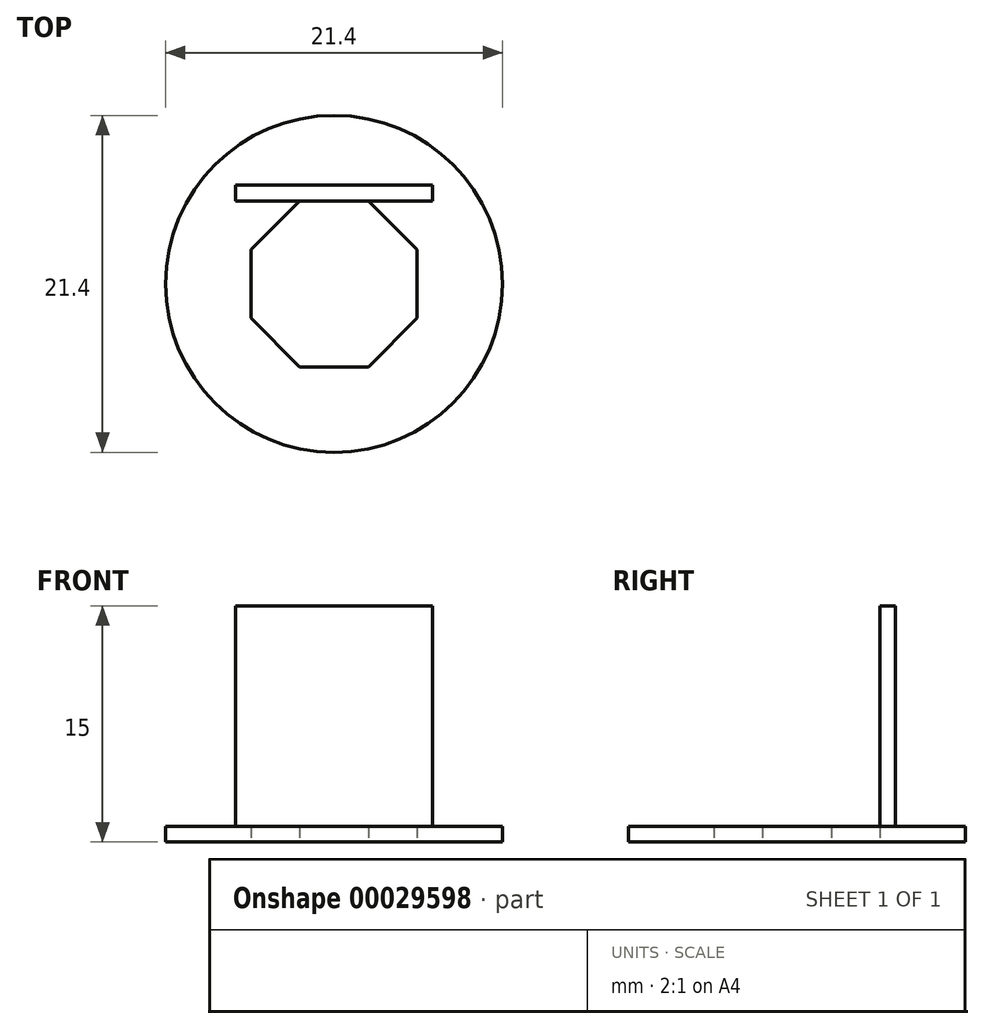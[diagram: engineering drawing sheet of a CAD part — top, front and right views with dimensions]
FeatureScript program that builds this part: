
annotation { "Feature Type Name" : "Feature", "Feature Type Description" : "" }
export const myFeature = defineFeature(function(context is Context, id is Id, definition is map)
    precondition{}
    {
        {
            var Q0;
            Q0=qCreatedBy(makeId("Top.planeOp"),FACE);
            var sketch = newSketch(context, id + "F0", { "sketchPlane" : qUnion([Q0])});
            skCircle(sketch, "E0", {"center": v(0, 0) * mm, "radius": 5.7 * mm});
            skCircle(sketch, "E1.0", {"center": v(0, 0) * mm, "radius": 10.7 * mm});
            skLineSegment(sketch, "E2", {"start": v(0, 5.7) * mm, "end": v(0, -5.7) * mm, "construction": true});
            skLineSegment(sketch, "E3", {"start": v(0, 0) * mm, "end": v(5.7, 0) * mm, "construction": true});
            skLineSegment(sketch, "E4", {"start": v(5.7, 0) * mm, "end": v(0, 5.7) * mm, "construction": true});
            skLineSegment(sketch, "E5", {"start": v(0, 0) * mm, "end": v(4.03, 4.03) * mm, "construction": true});
            skLineSegment(sketch, "E6", {"start": v(0, 5.7) * mm, "end": v(4.03, 4.03) * mm, "construction": true});
            skLineSegment(sketch, "E7", {"start": v(0, 0) * mm, "end": v(2.18, 5.27) * mm, "construction": true});
            skCircle(sketch, "E8.cCircle", {"center": v(0, 0) * mm, "radius": 5.7 * mm, "construction": true});
            skLineSegment(sketch, "E8.0", {"start": v(2.18, 5.27) * mm, "end": v(5.27, 2.18) * mm});
            skLineSegment(sketch, "E8.1", {"start": v(5.27, 2.18) * mm, "end": v(5.27, -2.18) * mm});
            skLineSegment(sketch, "E8.2", {"start": v(5.27, -2.18) * mm, "end": v(2.18, -5.27) * mm});
            skLineSegment(sketch, "E8.3", {"start": v(2.18, -5.27) * mm, "end": v(-2.18, -5.27) * mm});
            skLineSegment(sketch, "E8.4", {"start": v(-2.18, -5.27) * mm, "end": v(-5.27, -2.18) * mm});
            skLineSegment(sketch, "E8.5", {"start": v(-5.27, -2.18) * mm, "end": v(-5.27, 2.18) * mm});
            skLineSegment(sketch, "E8.6", {"start": v(-5.27, 2.18) * mm, "end": v(-2.18, 5.27) * mm});
            skLineSegment(sketch, "E8.7", {"start": v(-2.18, 5.27) * mm, "end": v(2.18, 5.27) * mm});
            skSolve(sketch);
        }
        {
            var Q0;
            {var subQ0=sQuery(id+"F0.wireOp",EDGE,"E8.6");Q0=makeQuery(id+"F0.imprint","IMPRINT",FACE,{"disambiguationData":[TD([[makeQuery(id+"F0.imprint","IMPRINT",EDGE,{"derivedFrom":subQ0}),1.0]])]});}
            var Q1;
            {var subQ0=sQuery(id+"F0.wireOp",EDGE,"E8.4");Q1=makeQuery(id+"F0.imprint","IMPRINT",FACE,{"disambiguationData":[TD([[makeQuery(id+"F0.imprint","IMPRINT",EDGE,{"derivedFrom":subQ0}),1.0]])]});}
            var Q2;
            {var subQ0=sQuery(id+"F0.wireOp",EDGE,"E8.3");Q2=makeQuery(id+"F0.imprint","IMPRINT",FACE,{"disambiguationData":[TD([[makeQuery(id+"F0.imprint","IMPRINT",EDGE,{"derivedFrom":subQ0}),1.0]])]});}
            var Q3;
            {var subQ0=sQuery(id+"F0.wireOp",EDGE,"E8.1");Q3=makeQuery(id+"F0.imprint","IMPRINT",FACE,{"disambiguationData":[TD([[makeQuery(id+"F0.imprint","IMPRINT",EDGE,{"derivedFrom":subQ0}),1.0]])]});}
            var Q4;
            Q4=makeQuery(id+"F0.imprint","IMPRINT",FACE,{"disambiguationData":[TD([[makeQuery(id+"F0.imprint","IMPRINT",EDGE,{"derivedFrom":sQuery(id+"F0.wireOp",EDGE,"E1.0")}),1.0]])]});
            var Q5;
            {var subQ0=sQuery(id+"F0.wireOp",EDGE,"E8.0");Q5=makeQuery(id+"F0.imprint","IMPRINT",FACE,{"disambiguationData":[TD([[makeQuery(id+"F0.imprint","IMPRINT",EDGE,{"derivedFrom":subQ0}),1.0]])]});}
            var Q6;
            {var subQ0=sQuery(id+"F0.wireOp",EDGE,"E8.7");Q6=makeQuery(id+"F0.imprint","IMPRINT",FACE,{"disambiguationData":[TD([[makeQuery(id+"F0.imprint","IMPRINT",EDGE,{"derivedFrom":subQ0}),1.0]])]});}
            var Q7;
            {var subQ0=sQuery(id+"F0.wireOp",EDGE,"E8.5");Q7=makeQuery(id+"F0.imprint","IMPRINT",FACE,{"disambiguationData":[TD([[makeQuery(id+"F0.imprint","IMPRINT",EDGE,{"derivedFrom":subQ0}),1.0]])]});}
            var Q8;
            {var subQ0=sQuery(id+"F0.wireOp",EDGE,"E8.2");Q8=makeQuery(id+"F0.imprint","IMPRINT",FACE,{"disambiguationData":[TD([[makeQuery(id+"F0.imprint","IMPRINT",EDGE,{"derivedFrom":subQ0}),1.0]])]});}
            extrude(context, id + "F1", {"entities" : qUnion([Q0, Q1, Q2, Q3, Q4, Q5, Q6, Q7, Q8]), "depth" : 1 * mm});
        }
        {
            var Q0;
            Q0=makeQuery(id+"F1.opExtrude","CAP_FACE",FACE,{"disambiguationData":[OSD([sQuery(id+"F0.wireOp",EDGE,"E1.0"),sQuery(id+"F0.wireOp",EDGE,"E8.0"),sQuery(id+"F0.wireOp",EDGE,"E8.1"),sQuery(id+"F0.wireOp",EDGE,"E8.2"),sQuery(id+"F0.wireOp",EDGE,"E8.3"),sQuery(id+"F0.wireOp",EDGE,"E8.4"),sQuery(id+"F0.wireOp",EDGE,"E8.5"),sQuery(id+"F0.wireOp",EDGE,"E8.6"),sQuery(id+"F0.wireOp",EDGE,"E8.7")])],"isStart":false});
            var sketch = newSketch(context, id + "F2", { "sketchPlane" : qUnion([Q0])});
            skLineSegment(sketch, "E9.bottom", {"start": v(-5.27, -2.18) * mm, "end": v(5.27, -2.18) * mm});
            skLineSegment(sketch, "E9.top", {"start": v(-5.27, 5.27) * mm, "end": v(5.27, 5.27) * mm});
            skLineSegment(sketch, "E9.left", {"start": v(-5.27, -2.18) * mm, "end": v(-5.27, 5.27) * mm});
            skLineSegment(sketch, "E9.right", {"start": v(5.27, -2.18) * mm, "end": v(5.27, 5.27) * mm});
            skLineSegment(sketch, "E10.0", {"start": v(6.27, -2.18) * mm, "end": v(6.27, 6.27) * mm});
            skLineSegment(sketch, "E10.1", {"start": v(-6.27, 6.27) * mm, "end": v(6.27, 6.27) * mm});
            skLineSegment(sketch, "E10.2", {"start": v(-6.27, -2.18) * mm, "end": v(-6.27, 6.27) * mm});
            skLineSegment(sketch, "E11", {"start": v(-6.27, -2.18) * mm, "end": v(-5.27, -2.18) * mm});
            skLineSegment(sketch, "E12", {"start": v(5.27, -2.18) * mm, "end": v(6.27, -2.18) * mm});
            skLineSegment(sketch, "E13", {"start": v(-5.27, 5.27) * mm, "end": v(-6.27, 5.27) * mm});
            skLineSegment(sketch, "E14", {"start": v(-6.27, 5.27) * mm, "end": v(6.27, 5.27) * mm});
            skSolve(sketch);
        }
        {
            var Q0;
            {var subQ7=sQuery(id+"F2.wireOp",EDGE,"E10.1");Q0=makeQuery(id+"F2.imprint","IMPRINT",FACE,{"disambiguationData":[TD([[makeQuery(id+"F2.imprint","IMPRINT",EDGE,{"derivedFrom":subQ7}),-1.0]])]});}
            extrude(context, id + "F3", {"entities" : qUnion([Q0]), "operationType" : NewBodyOperationType.ADD, "depth" : 14 * mm});
        }
    });
